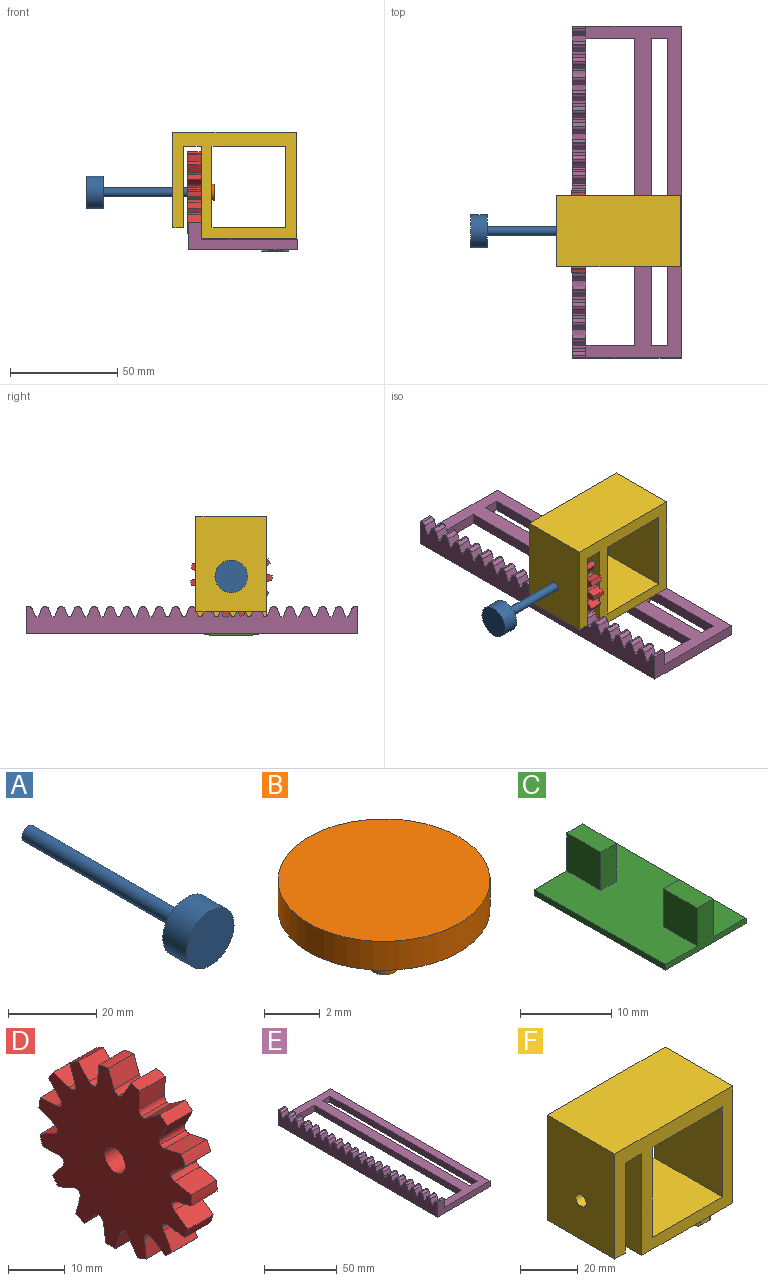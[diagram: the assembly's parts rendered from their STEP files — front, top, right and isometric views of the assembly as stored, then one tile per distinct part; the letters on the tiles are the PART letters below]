
ASSEMBLY  parts=6 mates=6
PART A: 7 faces, bbox 15.2x58.4x15.2 mm
  f0: plane 15.24x15.24mm, normal (0,-1,0), area 182.4mm2, adj f4
  f1: plane 4.06x4.06mm, normal (0,1,0), area 11.7mm2, adj f2,f5
  f2: cylinder r=2.03mm len=50.8mm, axis (0,1,0), area 648.6mm2, adj f1,f3
  f3: plane 15.24x15.24mm, normal (0,1,0), area 169.4mm2, adj f2,f4
  f4: cylinder r=7.62mm len=15.24mm, axis (0,1,0), area 364.8mm2, adj f0,f3
  f5: cylinder r=0.64mm len=5.08mm, axis (0,1,0), area 20.4mm2, adj f1,f6
  f6: plane 1.28x1.28mm, normal (0,1,0), area 1.3mm2, adj f5
PART B: 5 faces, bbox 7.6x7.6x3.8 mm
  f0: cylinder r=0.51mm len=2.54mm, axis (0,0,-1), area 8.1mm2, adj f1,f4
  f1: plane 1.02x1.02mm, normal (0,0,-1), area 0.8mm2, adj f0
  f2: cylinder r=3.81mm len=7.62mm, axis (0,0,-1), area 30.4mm2, adj f3,f4
  f3: plane 7.62x7.62mm, normal (0,0,1), area 45.6mm2, adj f2
  f4: plane 7.62x7.62mm, normal (0,0,-1), area 44.8mm2, adj f0,f2
PART C: 14 faces, bbox 12.6x20.2x5.8 mm
  f0: plane 20.17x12.61mm, normal (0,0,1), area 227mm2, adj f2,f3,f4,f5,f6,f7,f8,f10
  f1: plane 20.17x12.61mm, normal (0,0,-1), area 252.5mm2, adj f2,f3,f4,f5
  f2: plane 12.45x5.84mm, normal (0,-1,0), area 21.9mm2, adj f0,f1,f3,f5,f10,f12,f13
  f3: plane 20.17x0.76mm, normal (1,0,0), area 15.4mm2, adj f0,f1,f2,f4
  f4: plane 12.6x5.84mm, normal (0,1,0), area 22mm2, adj f0,f1,f3,f5,f6,f7,f9
  f5: plane 20.17x0.76mm, normal (-1,-0.01,0), area 15.4mm2, adj f0,f1,f2,f4
  f6: plane 5.23x5.08mm, normal (1,0,0), area 26.6mm2, adj f0,f4,f8,f9
  f7: plane 5.23x5.08mm, normal (-1,0,0), area 26.6mm2, adj f0,f4,f8,f9
  f8: plane 5.08x2.44mm, normal (0,-1,0), area 12.4mm2, adj f0,f6,f7,f9
  f9: plane 5.23x2.44mm, normal (0,0,1), area 12.7mm2, adj f4,f6,f7,f8
  f10: plane 5.23x5.08mm, normal (1,0,0), area 26.6mm2, adj f0,f2,f11,f13
  f11: plane 5.08x2.45mm, normal (0,1,0), area 12.4mm2, adj f0,f10,f12,f13
  f12: plane 5.23x5.08mm, normal (-1,0,0), area 26.6mm2, adj f0,f2,f11,f13
  f13: plane 5.23x2.45mm, normal (0,0,1), area 12.8mm2, adj f2,f10,f11,f12
PART D: 78 faces, bbox 6.4x38x38 mm
  f0: cylinder r=19.05mm len=6.35mm, axis (-1,0,0), area 14.8mm2, adj f3,f71,f72,f74
  f1: cylinder r=1.52mm len=6.35mm, axis (-1,0,0), area 9.5mm2, adj f2,f4,f71,f72
  f2: cylinder r=1.52mm len=6.35mm, axis (-1,0,0), area 8.1mm2, adj f1,f3,f71,f72
  f3: plane 6.35x4.18mm, normal (0,0.99,0.1), area 26.7mm2, adj f0,f2,f71,f72
  f4: plane 6.35x2.86mm, normal (0,-0.71,0.71), area 25.6mm2, adj f1,f5,f71,f72
  f5: cylinder r=19.05mm len=6.35mm, axis (-1,0,0), area 14.8mm2, adj f4,f8,f71,f72
  f6: cylinder r=1.52mm len=6.35mm, axis (-1,0,0), area 9.5mm2, adj f7,f9,f71,f72
  f7: cylinder r=1.52mm len=6.35mm, axis (-1,0,0), area 8.1mm2, adj f6,f8,f71,f72
  f8: plane 6.35x3.99mm, normal (0,0.95,-0.31), area 26.7mm2, adj f5,f7,f71,f72
  f9: plane 6.35x3.77mm, normal (0,-0.36,0.93), area 25.6mm2, adj f6,f10,f71,f72
  f10: cylinder r=19.05mm len=6.35mm, axis (-1,0,0), area 14.8mm2, adj f9,f13,f71,f72
  f11: cylinder r=1.52mm len=6.35mm, axis (-1,0,0), area 9.5mm2, adj f12,f14,f71,f72
  f12: cylinder r=1.52mm len=6.35mm, axis (-1,0,0), area 8.1mm2, adj f11,f13,f71,f72
  f13: plane 6.35x3.11mm, normal (0,0.74,-0.67), area 26.7mm2, adj f10,f12,f71,f72
  f14: plane 6.35x4.03mm, normal (0,0.05,1), area 25.6mm2, adj f11,f15,f71,f72
  f15: cylinder r=19.05mm len=6.35mm, axis (-1,0,0), area 14.8mm2, adj f14,f18,f71,f72
  f16: cylinder r=1.52mm len=6.35mm, axis (-1,0,0), area 9.5mm2, adj f17,f19,f71,f72
  f17: cylinder r=1.52mm len=6.35mm, axis (-1,0,0), area 8.1mm2, adj f16,f18,f71,f72
  f18: plane 6.35x3.84mm, normal (0,0.4,-0.91), area 26.7mm2, adj f15,f17,f71,f72
  f19: plane 6.35x3.59mm, normal (0,0.46,0.89), area 25.6mm2, adj f16,f20,f71,f72
  f20: cylinder r=19.05mm len=6.35mm, axis (-1,0,0), area 14.8mm2, adj f19,f23,f71,f72
  f21: cylinder r=1.52mm len=6.35mm, axis (-1,0,0), area 9.5mm2, adj f22,f24,f71,f72
  f22: cylinder r=1.52mm len=6.35mm, axis (-1,0,0), area 8.1mm2, adj f21,f23,f71,f72
  f23: plane 6.35x4.2mm, normal (0,0,-1), area 26.7mm2, adj f20,f22,f71,f72
  f24: plane 6.35x3.14mm, normal (0,0.78,0.63), area 25.6mm2, adj f21,f25,f71,f72
  f25: cylinder r=19.05mm len=6.35mm, axis (-1,0,0), area 14.8mm2, adj f24,f28,f71,f72
  f26: cylinder r=1.52mm len=6.35mm, axis (-1,0,0), area 9.5mm2, adj f27,f29,f71,f72
  f27: cylinder r=1.52mm len=6.35mm, axis (-1,0,0), area 8.1mm2, adj f26,f28,f71,f72
  f28: plane 6.35x3.83mm, normal (0,-0.41,-0.91), area 26.7mm2, adj f25,f27,f71,f72
  f29: plane 6.35x3.9mm, normal (0,0.97,0.26), area 25.6mm2, adj f26,f30,f71,f72
  f30: cylinder r=19.05mm len=6.35mm, axis (-1,0,0), area 14.8mm2, adj f29,f33,f71,f72
  f31: cylinder r=1.52mm len=6.35mm, axis (-1,0,0), area 9.5mm2, adj f32,f34,f71,f72
  f32: cylinder r=1.52mm len=6.35mm, axis (-1,0,0), area 8.1mm2, adj f31,f33,f71,f72
  f33: plane 6.35x3.13mm, normal (0,-0.75,-0.67), area 26.7mm2, adj f30,f32,f71,f72
  f34: plane 6.35x3.98mm, normal (0,0.99,-0.16), area 25.6mm2, adj f31,f35,f71,f72
  f35: cylinder r=19.05mm len=6.35mm, axis (-1,0,0), area 14.8mm2, adj f34,f38,f71,f72
  f36: cylinder r=1.52mm len=6.35mm, axis (-1,0,0), area 9.5mm2, adj f37,f39,f71,f72
  f37: cylinder r=1.52mm len=6.35mm, axis (-1,0,0), area 8.1mm2, adj f36,f38,f71,f72
  f38: plane 6.35x4mm, normal (0,-0.95,-0.31), area 26.7mm2, adj f35,f37,f71,f72
  f39: plane 6.35x3.38mm, normal (0,0.84,-0.55), area 25.6mm2, adj f36,f40,f71,f72
  f40: cylinder r=19.05mm len=6.35mm, axis (-1,0,0), area 14.8mm2, adj f39,f43,f71,f72
  f41: cylinder r=1.52mm len=6.35mm, axis (-1,0,0), area 9.5mm2, adj f42,f44,f71,f72
  f42: cylinder r=1.52mm len=6.35mm, axis (-1,0,0), area 8.1mm2, adj f41,f43,f71,f72
  f43: plane 6.35x4.17mm, normal (0,-0.99,0.11), area 26.7mm2, adj f40,f42,f71,f72
  f44: plane 6.35x3.39mm, normal (0,0.54,-0.84), area 25.6mm2, adj f41,f45,f71,f72
  f45: cylinder r=19.05mm len=6.35mm, axis (-1,0,0), area 14.8mm2, adj f44,f48,f71,f72
  f46: cylinder r=1.52mm len=6.35mm, axis (-1,0,0), area 9.5mm2, adj f47,f49,f71,f72
  f47: cylinder r=1.52mm len=6.35mm, axis (-1,0,0), area 8.1mm2, adj f46,f48,f71,f72
  f48: plane 6.35x3.63mm, normal (0,-0.86,0.5), area 26.7mm2, adj f45,f47,f71,f72
  f49: plane 6.35x3.99mm, normal (0,0.16,-0.99), area 25.6mm2, adj f46,f50,f71,f72
  f50: cylinder r=19.05mm len=6.35mm, axis (-1,0,0), area 14.8mm2, adj f49,f53,f71,f72
  f51: cylinder r=1.52mm len=6.35mm, axis (-1,0,0), area 9.5mm2, adj f52,f54,f71,f72
  f52: cylinder r=1.52mm len=6.35mm, axis (-1,0,0), area 8.1mm2, adj f51,f53,f71,f72
  f53: plane 6.35x3.4mm, normal (0,-0.59,0.81), area 26.7mm2, adj f50,f52,f71,f72
  f54: plane 6.35x3.9mm, normal (0,-0.26,-0.97), area 25.6mm2, adj f51,f55,f71,f72
  f55: cylinder r=19.05mm len=6.35mm, axis (-1,0,0), area 14.8mm2, adj f54,f58,f71,f72
  f56: cylinder r=1.52mm len=6.35mm, axis (-1,0,0), area 9.5mm2, adj f57,f59,f71,f72
  f57: cylinder r=1.52mm len=6.35mm, axis (-1,0,0), area 8.1mm2, adj f56,f58,f71,f72
  f58: plane 6.35x4.11mm, normal (0,-0.2,0.98), area 26.7mm2, adj f55,f57,f71,f72
  f59: plane 6.35x3.13mm, normal (0,-0.63,-0.78), area 25.6mm2, adj f56,f60,f71,f72
  f60: cylinder r=19.05mm len=6.35mm, axis (-1,0,0), area 14.8mm2, adj f59,f63,f71,f72
  f61: cylinder r=1.52mm len=6.35mm, axis (-1,0,0), area 9.5mm2, adj f62,f64,f71,f72
  f62: cylinder r=1.52mm len=6.35mm, axis (-1,0,0), area 8.1mm2, adj f61,f63,f71,f72
  f63: plane 6.35x4.1mm, normal (0,0.21,0.98), area 26.7mm2, adj f60,f62,f71,f72
  f64: plane 6.35x3.6mm, normal (0,-0.89,-0.45), area 25.6mm2, adj f61,f65,f71,f72
  f65: cylinder r=19.05mm len=6.35mm, axis (-1,0,0), area 14.8mm2, adj f64,f68,f71,f72
  f66: cylinder r=1.52mm len=6.35mm, axis (-1,0,0), area 9.5mm2, adj f67,f69,f71,f72
  f67: cylinder r=1.52mm len=6.35mm, axis (-1,0,0), area 8.1mm2, adj f66,f68,f71,f72
  f68: plane 6.35x3.39mm, normal (0,0.59,0.81), area 26.7mm2, adj f65,f67,f71,f72
  f69: plane 6.35x4.03mm, normal (0,-1,-0.05), area 25.6mm2, adj f66,f70,f71,f72
  f70: cylinder r=19.05mm len=6.35mm, axis (-1,0,0), area 14.8mm2, adj f69,f71,f72,f73
  f71: plane 38.02x38mm, normal (1,0,0), area 875.4mm2, adj f0,f1,f2,f3,f4,f5,f6,f7
  f72: plane 38.02x38mm, normal (-1,0,0), area 875.4mm2, adj f0,f1,f2,f3,f4,f5,f6,f7
  f73: plane 6.35x3.64mm, normal (0,0.87,0.5), area 26.7mm2, adj f70,f71,f72,f76
  f74: plane 6.35x3.76mm, normal (0,-0.93,0.36), area 25.6mm2, adj f0,f71,f72,f75
  f75: cylinder r=1.52mm len=6.35mm, axis (-1,0,0), area 9.5mm2, adj f71,f72,f74,f76
  f76: cylinder r=1.52mm len=6.35mm, axis (-1,0,0), area 8.1mm2, adj f71,f72,f73,f75
  f77: cylinder r=2.54mm len=6.35mm, axis (1,0,0), area 101.3mm2, adj f71,f72
PART E: 142 faces, bbox 50.8x154.9x12.7 mm
  f0: plane 22.86x5.08mm, normal (0,1,0), area 116.1mm2, adj f14,f17,f19,f86
  f1: plane 7.62x5.08mm, normal (0,1,0), area 38.7mm2, adj f3,f14,f19,f87
  f2: plane 7.62x5.08mm, normal (0,-1,0), area 38.7mm2, adj f3,f14,f19,f87
  f3: plane 142.95x5.08mm, normal (-1,0,0), area 726.2mm2, adj f1,f2,f14,f19
  f4: plane 6.35x0.14mm, normal (0,0,1), area 0.9mm2, adj f15,f17,f122,f125
  f5: plane 6.35x0.14mm, normal (0,0,1), area 0.9mm2, adj f15,f17,f119,f124
  f6: plane 6.35x0.14mm, normal (0,0,1), area 0.9mm2, adj f15,f17,f123,f126
  f7: plane 6.35x0.14mm, normal (0,0,1), area 0.9mm2, adj f15,f17,f127,f128
  f8: plane 6.35x0.14mm, normal (0,0,1), area 0.9mm2, adj f15,f17,f129,f130
  f9: plane 6.35x0.14mm, normal (0,0,1), area 0.9mm2, adj f15,f17,f131,f132
  f10: plane 6.35x0.14mm, normal (0,0,1), area 0.9mm2, adj f15,f17,f133,f134
  f11: plane 6.35x0.14mm, normal (0,0,1), area 0.9mm2, adj f15,f17,f135,f136
  f12: plane 6.35x0.14mm, normal (0,0,1), area 0.9mm2, adj f15,f17,f137,f139
  f13: plane 6.35x0.14mm, normal (0,0,1), area 0.9mm2, adj f15,f17,f138,f141
  f14: plane 154.94x44.45mm, normal (0,0,1), area 2529.9mm2, adj f0,f1,f2,f3,f16,f17,f18,f55
  f15: plane 154.94x12.7mm, normal (-1,0,0), area 1659.6mm2, adj f4,f5,f6,f7,f8,f9,f10,f11
  f16: plane 50.8x12.7mm, normal (0,-1,0), area 306.5mm2, adj f14,f15,f17,f18,f19,f20
  f17: plane 154.94x12.7mm, normal (1,0,0), area 1598.7mm2, adj f0,f4,f5,f6,f7,f8,f9,f10
  f18: plane 154.94x5.08mm, normal (1,0,0), area 787.1mm2, adj f14,f16,f19,f55
  f19: plane 154.94x50.8mm, normal (0,0,-1), area 3513.8mm2, adj f0,f1,f2,f3,f15,f16,f17,f18
  f20: plane 6.35x1.34mm, normal (0,0,1), area 8.5mm2, adj f15,f16,f17,f140
  f21: plane 6.35x3.6mm, normal (0,0.93,0.37), area 24.6mm2, adj f15,f17,f23,f140
  f22: plane 6.35x3.6mm, normal (0,-0.93,0.37), area 24.6mm2, adj f15,f17,f23,f141
  f23: plane 6.35x1.27mm, normal (0,0,1), area 8.1mm2, adj f15,f17,f21,f22
  f24: plane 6.35x3.6mm, normal (0,0.93,0.37), area 24.6mm2, adj f15,f17,f26,f138
  f25: plane 6.35x3.6mm, normal (0,-0.93,0.37), area 24.6mm2, adj f15,f17,f26,f139
  f26: plane 6.35x1.27mm, normal (0,0,1), area 8.1mm2, adj f15,f17,f24,f25
  f27: plane 6.35x3.6mm, normal (0,0.93,0.37), area 24.6mm2, adj f15,f17,f29,f137
  f28: plane 6.35x3.6mm, normal (0,-0.93,0.37), area 24.6mm2, adj f15,f17,f29,f136
  f29: plane 6.35x1.27mm, normal (0,0,1), area 8.1mm2, adj f15,f17,f27,f28
  f30: plane 6.35x3.6mm, normal (0,0.93,0.37), area 24.6mm2, adj f15,f17,f32,f135
  f31: plane 6.35x3.6mm, normal (0,-0.93,0.37), area 24.6mm2, adj f15,f17,f32,f134
  f32: plane 6.35x1.27mm, normal (0,0,1), area 8.1mm2, adj f15,f17,f30,f31
  f33: plane 6.35x3.6mm, normal (0,0.93,0.37), area 24.6mm2, adj f15,f17,f35,f133
  f34: plane 6.35x3.6mm, normal (0,-0.93,0.37), area 24.6mm2, adj f15,f17,f35,f132
  f35: plane 6.35x1.27mm, normal (0,0,1), area 8.1mm2, adj f15,f17,f33,f34
  f36: plane 6.35x2.96mm, normal (0,0.93,0.37), area 20.3mm2, adj f15,f17,f100,f131
  f37: plane 6.35x2.96mm, normal (0,-0.93,0.37), area 20.3mm2, adj f15,f17,f101,f130
  f38: plane 6.35x2.96mm, normal (0,0.93,0.37), area 20.3mm2, adj f15,f17,f98,f129
  f39: plane 6.35x2.96mm, normal (0,-0.93,0.37), area 20.3mm2, adj f15,f17,f99,f128
  f40: plane 6.35x2.96mm, normal (0,0.93,0.37), area 20.3mm2, adj f15,f17,f96,f127
  f41: plane 6.35x2.96mm, normal (0,-0.93,0.37), area 20.3mm2, adj f15,f17,f97,f126
  f42: plane 6.35x2.96mm, normal (0,0.93,0.37), area 20.3mm2, adj f15,f17,f94,f125
  f43: plane 6.35x2.96mm, normal (0,-0.93,0.37), area 20.3mm2, adj f15,f17,f95,f124
  f44: plane 6.35x2.96mm, normal (0,0.93,0.37), area 20.3mm2, adj f15,f17,f92,f123
  f45: plane 6.35x2.96mm, normal (0,-0.93,0.37), area 20.3mm2, adj f15,f17,f93,f122
  f46: plane 6.35x0.14mm, normal (0,0,1), area 0.9mm2, adj f15,f17,f103,f118
  f47: plane 6.35x0.14mm, normal (0,0,1), area 0.9mm2, adj f15,f17,f102,f117
  f48: plane 6.35x0.14mm, normal (0,0,1), area 0.9mm2, adj f15,f17,f115,f116
  f49: plane 6.35x0.14mm, normal (0,0,1), area 0.9mm2, adj f15,f17,f113,f114
  f50: plane 6.35x0.14mm, normal (0,0,1), area 0.9mm2, adj f15,f17,f111,f112
  f51: plane 6.35x0.14mm, normal (0,0,1), area 0.9mm2, adj f15,f17,f109,f110
  f52: plane 6.35x0.14mm, normal (0,0,1), area 0.9mm2, adj f15,f17,f107,f108
  f53: plane 6.35x0.14mm, normal (0,0,1), area 0.9mm2, adj f15,f17,f104,f106
  f54: plane 6.35x0.14mm, normal (0,0,1), area 0.9mm2, adj f15,f17,f105,f120
  f55: plane 50.8x12.7mm, normal (0,1,0), area 306.5mm2, adj f14,f15,f17,f18,f19,f57
  f56: plane 22.86x5.08mm, normal (0,-1,0), area 116.1mm2, adj f14,f17,f19,f86
  f57: plane 6.35x1.34mm, normal (0,0,1), area 8.5mm2, adj f15,f17,f55,f121
  f58: plane 6.35x3.6mm, normal (0,-0.93,0.37), area 24.6mm2, adj f15,f17,f60,f121
  f59: plane 6.35x3.6mm, normal (0,0.93,0.37), area 24.6mm2, adj f15,f17,f60,f120
  f60: plane 6.35x1.27mm, normal (0,0,1), area 8.1mm2, adj f15,f17,f58,f59
  f61: plane 6.35x3.6mm, normal (0,-0.93,0.37), area 24.6mm2, adj f15,f17,f63,f105
  f62: plane 6.35x3.6mm, normal (0,0.93,0.37), area 24.6mm2, adj f15,f17,f63,f104
  f63: plane 6.35x1.27mm, normal (0,0,1), area 8.1mm2, adj f15,f17,f61,f62
  f64: plane 6.35x3.6mm, normal (0,-0.93,0.37), area 24.6mm2, adj f15,f17,f66,f106
  f65: plane 6.35x3.6mm, normal (0,0.93,0.37), area 24.6mm2, adj f15,f17,f66,f107
  f66: plane 6.35x1.27mm, normal (0,0,1), area 8.1mm2, adj f15,f17,f64,f65
  f67: plane 6.35x3.6mm, normal (0,-0.93,0.37), area 24.6mm2, adj f15,f17,f69,f108
  f68: plane 6.35x3.6mm, normal (0,0.93,0.37), area 24.6mm2, adj f15,f17,f69,f109
  f69: plane 6.35x1.27mm, normal (0,0,1), area 8.1mm2, adj f15,f17,f67,f68
  f70: plane 6.35x3.6mm, normal (0,-0.93,0.37), area 24.6mm2, adj f15,f17,f72,f110
  f71: plane 6.35x3.6mm, normal (0,0.93,0.37), area 24.6mm2, adj f15,f17,f72,f111
  f72: plane 6.35x1.27mm, normal (0,0,1), area 8.1mm2, adj f15,f17,f70,f71
  f73: plane 6.35x3.6mm, normal (0,-0.93,0.37), area 24.6mm2, adj f15,f17,f75,f112
  f74: plane 6.35x3.6mm, normal (0,0.93,0.37), area 24.6mm2, adj f15,f17,f75,f113
  f75: plane 6.35x1.27mm, normal (0,0,1), area 8.1mm2, adj f15,f17,f73,f74
  f76: plane 6.35x3.6mm, normal (0,-0.93,0.37), area 24.6mm2, adj f15,f17,f78,f114
  f77: plane 6.35x3.6mm, normal (0,0.93,0.37), area 24.6mm2, adj f15,f17,f78,f115
  f78: plane 6.35x1.27mm, normal (0,0,1), area 8.1mm2, adj f15,f17,f76,f77
  f79: plane 6.35x3.6mm, normal (0,-0.93,0.37), area 24.6mm2, adj f15,f17,f81,f116
  f80: plane 6.35x3.6mm, normal (0,0.93,0.37), area 24.6mm2, adj f15,f17,f81,f117
  f81: plane 6.35x1.27mm, normal (0,0,1), area 8.1mm2, adj f15,f17,f79,f80
  f82: plane 6.35x2.96mm, normal (0,-0.93,0.37), area 20.3mm2, adj f15,f17,f91,f118
  f83: plane 6.35x2.96mm, normal (0,0.93,0.37), area 20.3mm2, adj f15,f17,f90,f119
  f84: plane 6.35x2.96mm, normal (0,-0.93,0.37), area 20.3mm2, adj f15,f17,f89,f102
  f85: plane 6.35x2.96mm, normal (0,0.93,0.37), area 20.3mm2, adj f15,f17,f88,f103
  f86: plane 142.95x5.08mm, normal (-1,0,0), area 726.2mm2, adj f0,f14,f19,f56
  f87: plane 142.95x5.08mm, normal (1,0,0), area 726.2mm2, adj f1,f2,f14,f19
  f88: cylinder r=1.02mm len=6.35mm, axis (-1,0,0), area 7.3mm2, adj f15,f17,f85,f89
  f89: cylinder r=1.02mm len=6.35mm, axis (1,0,0), area 7.3mm2, adj f15,f17,f84,f88
  f90: cylinder r=1.02mm len=6.35mm, axis (-1,0,0), area 7.3mm2, adj f15,f17,f83,f91
  f91: cylinder r=1.02mm len=6.35mm, axis (-1,0,0), area 7.3mm2, adj f15,f17,f82,f90
  f92: cylinder r=1.02mm len=6.35mm, axis (1,0,0), area 7.3mm2, adj f15,f17,f44,f93
  f93: cylinder r=1.02mm len=6.35mm, axis (-1,0,0), area 7.3mm2, adj f15,f17,f45,f92
  f94: cylinder r=1.02mm len=6.35mm, axis (-1,0,0), area 7.3mm2, adj f15,f17,f42,f95
  f95: cylinder r=1.02mm len=6.35mm, axis (-1,0,0), area 7.3mm2, adj f15,f17,f43,f94
  f96: cylinder r=1.02mm len=6.35mm, axis (-1,0,0), area 7.3mm2, adj f15,f17,f40,f97
  f97: cylinder r=1.02mm len=6.35mm, axis (-1,0,0), area 7.3mm2, adj f15,f17,f41,f96
  f98: cylinder r=1.02mm len=6.35mm, axis (-1,0,0), area 7.3mm2, adj f15,f17,f38,f99
  f99: cylinder r=1.02mm len=6.35mm, axis (-1,0,0), area 7.3mm2, adj f15,f17,f39,f98
  f100: cylinder r=1.02mm len=6.35mm, axis (-1,0,0), area 7.3mm2, adj f15,f17,f36,f101
  f101: cylinder r=1.02mm len=6.35mm, axis (-1,0,0), area 7.3mm2, adj f15,f17,f37,f100
  f102: cylinder r=1.78mm len=6.35mm, axis (-1,0,0), area 13.4mm2, adj f15,f17,f47,f84
  f103: cylinder r=1.78mm len=6.35mm, axis (1,0,0), area 13.4mm2, adj f15,f17,f46,f85
  f104: cylinder r=1.78mm len=6.35mm, axis (-1,0,0), area 13.4mm2, adj f15,f17,f53,f62
  f105: cylinder r=1.78mm len=6.35mm, axis (-1,0,0), area 13.4mm2, adj f15,f17,f54,f61
  f106: cylinder r=1.78mm len=6.35mm, axis (-1,0,0), area 13.4mm2, adj f15,f17,f53,f64
  f107: cylinder r=1.78mm len=6.35mm, axis (-1,0,0), area 13.4mm2, adj f15,f17,f52,f65
  f108: cylinder r=1.78mm len=6.35mm, axis (-1,0,0), area 13.4mm2, adj f15,f17,f52,f67
  f109: cylinder r=1.78mm len=6.35mm, axis (-1,0,0), area 13.4mm2, adj f15,f17,f51,f68
  f110: cylinder r=1.78mm len=6.35mm, axis (-1,0,0), area 13.4mm2, adj f15,f17,f51,f70
  f111: cylinder r=1.78mm len=6.35mm, axis (-1,0,0), area 13.4mm2, adj f15,f17,f50,f71
  f112: cylinder r=1.78mm len=6.35mm, axis (-1,0,0), area 13.4mm2, adj f15,f17,f50,f73
  f113: cylinder r=1.78mm len=6.35mm, axis (-1,0,0), area 13.4mm2, adj f15,f17,f49,f74
  f114: cylinder r=1.78mm len=6.35mm, axis (-1,0,0), area 13.4mm2, adj f15,f17,f49,f76
  f115: cylinder r=1.78mm len=6.35mm, axis (-1,0,0), area 13.4mm2, adj f15,f17,f48,f77
  f116: cylinder r=1.78mm len=6.35mm, axis (-1,0,0), area 13.4mm2, adj f15,f17,f48,f79
  f117: cylinder r=1.78mm len=6.35mm, axis (-1,0,0), area 13.4mm2, adj f15,f17,f47,f80
  f118: cylinder r=1.78mm len=6.35mm, axis (-1,0,0), area 13.4mm2, adj f15,f17,f46,f82
  f119: cylinder r=1.78mm len=6.35mm, axis (-1,0,0), area 13.4mm2, adj f5,f15,f17,f83
  f120: cylinder r=1.78mm len=6.35mm, axis (-1,0,0), area 13.4mm2, adj f15,f17,f54,f59
  f121: cylinder r=1.78mm len=6.35mm, axis (-1,0,0), area 13.4mm2, adj f15,f17,f57,f58
  f122: cylinder r=1.78mm len=6.35mm, axis (1,0,0), area 13.4mm2, adj f4,f15,f17,f45
  f123: cylinder r=1.78mm len=6.35mm, axis (-1,0,0), area 13.4mm2, adj f6,f15,f17,f44
  f124: cylinder r=1.78mm len=6.35mm, axis (-1,0,0), area 13.4mm2, adj f5,f15,f17,f43
  f125: cylinder r=1.78mm len=6.35mm, axis (-1,0,0), area 13.4mm2, adj f4,f15,f17,f42
  f126: cylinder r=1.78mm len=6.35mm, axis (-1,0,0), area 13.4mm2, adj f6,f15,f17,f41
  f127: cylinder r=1.78mm len=6.35mm, axis (-1,0,0), area 13.4mm2, adj f7,f15,f17,f40
  f128: cylinder r=1.78mm len=6.35mm, axis (-1,0,0), area 13.4mm2, adj f7,f15,f17,f39
  f129: cylinder r=1.78mm len=6.35mm, axis (-1,0,0), area 13.4mm2, adj f8,f15,f17,f38
  f130: cylinder r=1.78mm len=6.35mm, axis (-1,0,0), area 13.4mm2, adj f8,f15,f17,f37
  f131: cylinder r=1.78mm len=6.35mm, axis (-1,0,0), area 13.4mm2, adj f9,f15,f17,f36
  f132: cylinder r=1.78mm len=6.35mm, axis (-1,0,0), area 13.4mm2, adj f9,f15,f17,f34
  f133: cylinder r=1.78mm len=6.35mm, axis (-1,0,0), area 13.4mm2, adj f10,f15,f17,f33
  f134: cylinder r=1.78mm len=6.35mm, axis (-1,0,0), area 13.4mm2, adj f10,f15,f17,f31
  f135: cylinder r=1.78mm len=6.35mm, axis (-1,0,0), area 13.4mm2, adj f11,f15,f17,f30
  f136: cylinder r=1.78mm len=6.35mm, axis (-1,0,0), area 13.4mm2, adj f11,f15,f17,f28
  f137: cylinder r=1.78mm len=6.35mm, axis (-1,0,0), area 13.4mm2, adj f12,f15,f17,f27
  f138: cylinder r=1.78mm len=6.35mm, axis (-1,0,0), area 13.4mm2, adj f13,f15,f17,f24
  f139: cylinder r=1.78mm len=6.35mm, axis (-1,0,0), area 13.4mm2, adj f12,f15,f17,f25
  f140: cylinder r=1.78mm len=6.35mm, axis (-1,0,0), area 13.4mm2, adj f15,f17,f20,f21
  f141: cylinder r=1.78mm len=6.35mm, axis (-1,0,0), area 13.4mm2, adj f13,f15,f17,f22
PART F: 35 faces, bbox 57.7x33x55 mm
  f0: plane 25.4x6.86mm, normal (0,0,-1), area 147mm2, adj f1,f2,f3,f4,f5,f6,f7,f8
  f1: plane 22.86x5.46mm, normal (-1,0,0), area 124.8mm2, adj f0,f13,f16,f23
  f2: plane 5.46x4.32mm, normal (0,-1,0), area 23.6mm2, adj f0,f15,f16,f23
  f3: plane 22.86x5.46mm, normal (1,0,0), area 124.8mm2, adj f0,f14,f15,f23
  f4: plane 5.46x2.46mm, normal (0,1,0), area 13.5mm2, adj f0,f5,f7,f24
  f5: plane 5.46x5.24mm, normal (1,0,0), area 28.6mm2, adj f0,f4,f6,f24
  f6: plane 5.46x2.46mm, normal (0,-1,0), area 13.5mm2, adj f0,f5,f7,f24
  f7: plane 5.46x5.24mm, normal (-1,0,0), area 28.6mm2, adj f0,f4,f6,f24
  f8: plane 5.46x4.32mm, normal (0,1,0), area 23.6mm2, adj f0,f13,f14,f23
  f9: plane 5.46x2.46mm, normal (0,-1,0), area 13.5mm2, adj f0,f10,f12,f17
  f10: plane 5.46x5.24mm, normal (1,0,0), area 28.6mm2, adj f0,f9,f11,f17
  f11: plane 5.46x2.46mm, normal (0,1,0), area 13.5mm2, adj f0,f10,f12,f17
  f12: plane 5.46x5.24mm, normal (-1,0,0), area 28.6mm2, adj f0,f9,f11,f17
  f13: cylinder r=1.27mm len=5.46mm, axis (0,0,-1), area 10.9mm2, adj f0,f1,f8,f23
  f14: cylinder r=1.27mm len=5.46mm, axis (0,0,1), area 10.9mm2, adj f0,f3,f8,f23
  f15: cylinder r=1.27mm len=5.46mm, axis (0,0,1), area 10.9mm2, adj f0,f2,f3,f23
  f16: cylinder r=1.27mm len=5.46mm, axis (0,0,-1), area 10.9mm2, adj f0,f1,f2,f23
  f17: plane 5.24x2.46mm, normal (0,0,-1), area 12.9mm2, adj f9,f10,f11,f12
  f18: plane 34.29x33.02mm, normal (0,0,1), area 1132.3mm2, adj f20,f22,f25,f26
  f19: plane 43.18x33.02mm, normal (-1,0,0), area 1405.5mm2, adj f20,f22,f23,f28,f31
  f20: plane 57.66x49.53mm, normal (0,1,0), area 1172.1mm2, adj f18,f19,f21,f23,f25,f26,f27,f28
  f21: plane 49.53x33.02mm, normal (1,0,0), area 1635.5mm2, adj f20,f22,f23,f30
  f22: plane 57.66x49.53mm, normal (0,-1,0), area 1172.1mm2, adj f18,f19,f21,f23,f25,f26,f27,f28
  f23: plane 44.45x33.02mm, normal (0,0,-1), area 1294.9mm2, adj f1,f2,f3,f8,f13,f14,f15,f16
  f24: plane 5.24x2.46mm, normal (0,0,-1), area 12.9mm2, adj f4,f5,f6,f7
  f25: plane 38.1x33.02mm, normal (1,0,0), area 1237.8mm2, adj f18,f20,f22,f27,f31
  f26: plane 38.1x33.02mm, normal (-1,0,0), area 1258.1mm2, adj f18,f20,f22,f27
  f27: plane 34.29x33.02mm, normal (0,0,-1), area 1132.3mm2, adj f20,f22,f25,f26
  f28: plane 33.02x8.14mm, normal (0,0,-1), area 268.8mm2, adj f19,f20,f22,f32
  f29: plane 44.45x33.02mm, normal (-1,0,0), area 1447.5mm2, adj f20,f22,f30,f33,f34
  f30: plane 57.66x33.02mm, normal (0,0,1), area 1903.9mm2, adj f20,f21,f22,f29
  f31: cylinder r=2.54mm len=5.08mm, axis (-1,0,0), area 81.1mm2, adj f19,f25
  f32: plane 38.1x33.02mm, normal (1,0,0), area 1237.8mm2, adj f20,f22,f28,f33,f34
  f33: plane 33.02x5.07mm, normal (0,0,-1), area 167.4mm2, adj f20,f22,f29,f32
  f34: cylinder r=2.54mm len=5.08mm, axis (-1,0,0), area 80.9mm2, adj f29,f32
PLACE A rot(axis=(0.25,0.25,-0.94),93.7deg) t=(-68.25,-105.82,42.31)mm
PLACE B rot(axis=(-0.45,0.77,-0.45),104.7deg) t=(-19.4,-70.63,62.24)mm
PLACE C t=(11.52,-50.53,34.62)mm
PLACE D rot(axis=(0,-0.5,-0.86),180deg) t=(-21.94,-70.63,62.24)mm
PLACE E t=(40.13,-53.56,35.38)mm fixed
PLACE F t=(12.73,-70.63,35.19)mm
MATE slider F.f8 <-> E.f2  axis (0,1,0) through (12.73,-57.93,37.92)mm
MATE slider D.f0 <-> A.f2  axis (-1,0,0) through (-28.29,-70.63,62.24)mm
MATE fastened C.f8 <-> F.f11  axis (0,-1,0) through (12.74,-65.81,37.92)mm
MATE revolute F.f31 <-> A.f2  axis (1,0,0) through (-16.86,-70.63,62.24)mm
MATE fastened A.f2 <-> B.f2  axis (1,0,0) through (-16.86,-70.63,62.24)mm
MATE revolute D.f77 <-> F.f31  axis (1,0,0) through (-21.94,-70.63,62.24)mm
